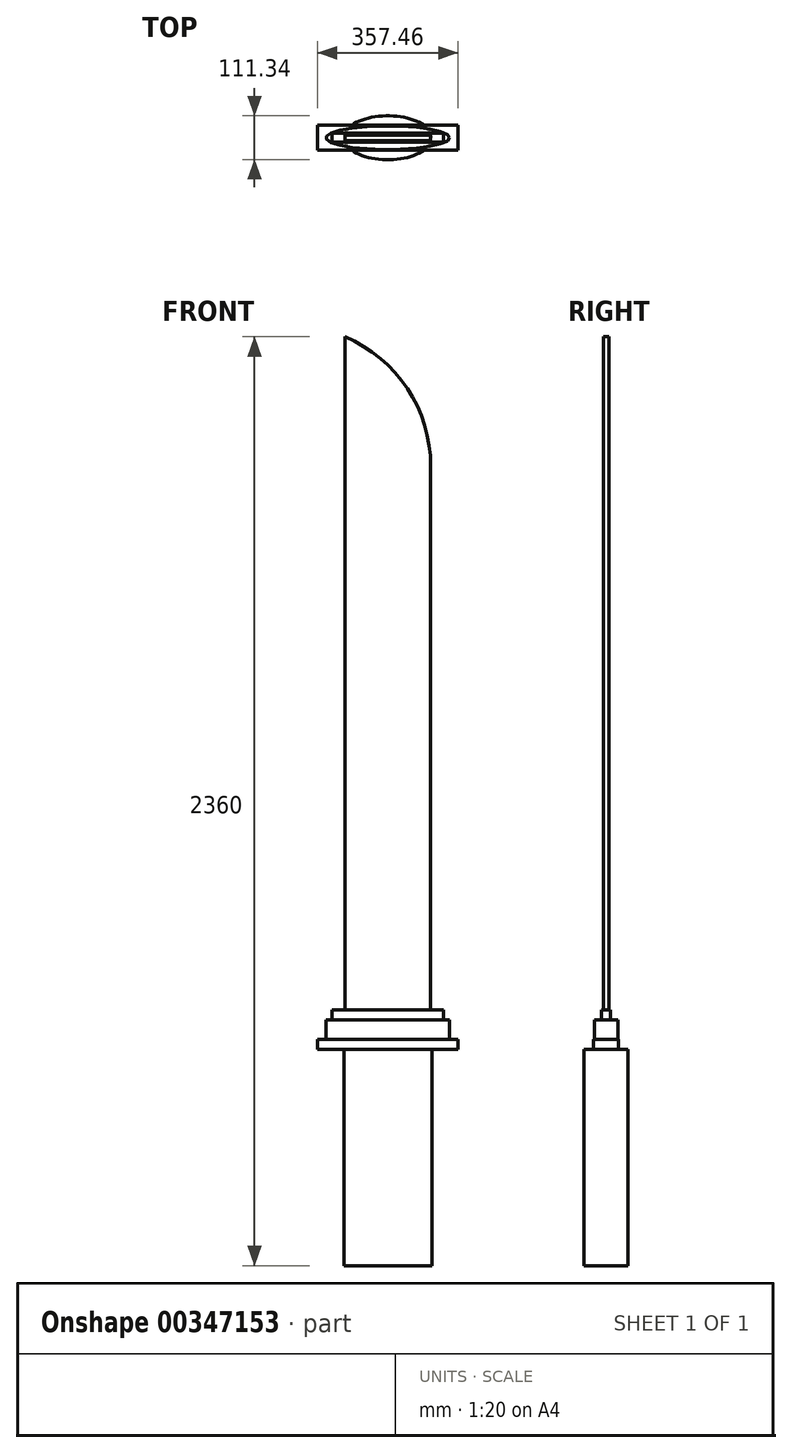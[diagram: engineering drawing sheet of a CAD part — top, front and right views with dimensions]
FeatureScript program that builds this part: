
annotation { "Feature Type Name" : "Feature", "Feature Type Description" : "" }
export const myFeature = defineFeature(function(context is Context, id is Id, definition is map)
    precondition{}
    {
        {
            var Q0;
            Q0=qCreatedBy(makeId("Top.planeOp"),FACE);
            var sketch = newSketch(context, id + "F0", { "sketchPlane" : qUnion([Q0])});
            skLineSegment(sketch, "E0.bottom", {"start": v(108.9, 6.8) * mm, "end": v(-108.9, 6.8) * mm});
            skLineSegment(sketch, "E0.top", {"start": v(108.9, -6.8) * mm, "end": v(-108.9, -6.8) * mm});
            skLineSegment(sketch, "E0.left", {"start": v(108.9, 6.8) * mm, "end": v(108.9, -6.8) * mm});
            skLineSegment(sketch, "E0.right", {"start": v(-108.9, 6.8) * mm, "end": v(-108.9, -6.8) * mm});
            skPoint(sketch, "E0.middle", {"position": v(0, 0) * mm});
            skSolve(sketch);
        }
        {
            var Q0;
            Q0=makeQuery(id+"F0.imprint","IMPRINT",FACE,{"disambiguationData":[TD([[makeQuery(id+"F0.imprint","IMPRINT",EDGE,{"derivedFrom":sQuery(id+"F0.wireOp",EDGE,"E0.bottom")}),1.0]])]});
            extrude(context, id + "F1", {"entities" : qUnion([Q0]), "depth" : 1710 * mm});
        }
        {
            var Q0;
            Q0=makeQuery(id+"F1.opExtrude","CAP_EDGE",EDGE,{"disambiguationData":[OSD([sQuery(id+"F0.wireOp",EDGE,"E0.left")])],"isStart":false});
            fillet(context, id + "F2", {"entities" : qUnion([Q0]), "radius" : 357.3 * mm, "tangentPropagation" : true, "allowEdgeOverflow" : false});
        }
        {
            var Q0;
            Q0=qCreatedBy(makeId("Top.planeOp"),FACE);
            var sketch = newSketch(context, id + "F3", { "sketchPlane" : qUnion([Q0])});
            skLineSegment(sketch, "E1.bottom", {"start": v(142.01, 11.57) * mm, "end": v(-142.01, 11.57) * mm});
            skLineSegment(sketch, "E1.top", {"start": v(142.01, -11.57) * mm, "end": v(-142.01, -11.57) * mm});
            skLineSegment(sketch, "E1.left", {"start": v(142.01, 11.57) * mm, "end": v(142.01, -11.57) * mm});
            skLineSegment(sketch, "E1.right", {"start": v(-142.01, 11.57) * mm, "end": v(-142.01, -11.57) * mm});
            skPoint(sketch, "E1.middle", {"position": v(0, 0) * mm});
            skSolve(sketch);
        }
        {
            var Q0;
            Q0=makeQuery(id+"F3.imprint","IMPRINT",FACE,{"disambiguationData":[TD([[makeQuery(id+"F3.imprint","IMPRINT",EDGE,{"derivedFrom":sQuery(id+"F3.wireOp",EDGE,"E1.bottom")}),1.0]])]});
            extrude(context, id + "F4", {"entities" : qUnion([Q0]), "operationType" : NewBodyOperationType.ADD, "oppositeDirection" : true, "depth" : 25 * mm});
        }
        {
            var Q0;
            Q0=qCreatedBy(makeId("Top.planeOp"),FACE);
            cPlane(context, id + "F5", {"entities" : qUnion([Q0]), "cplaneType" : CPlaneType.OFFSET, "offset" : 25 * mm, "oppositeDirection" : true, "width" : 150 * mm, "height" : 150 * mm});
        }
        {
            var Q0;
            Q0=qCreatedBy(id+"F5.planeOp",FACE);
            var sketch = newSketch(context, id + "F6", { "sketchPlane" : qUnion([Q0])});
            skEllipse(sketch, "E2", {"center": v(0, 0) * mm, "majorRadius": 157.13 * mm, "minorRadius": 29.95 * mm, "majorAxis": v(1, 0)});
            skSolve(sketch);
        }
        {
            var Q0;
            Q0=makeQuery(id+"F6.imprint","IMPRINT",FACE,{"disambiguationData":[TD([[makeQuery(id+"F6.imprint","IMPRINT",EDGE,{"derivedFrom":sQuery(id+"F6.wireOp",EDGE,"E2")}),1.0]])]});
            extrude(context, id + "F7", {"entities" : qUnion([Q0]), "operationType" : NewBodyOperationType.ADD, "oppositeDirection" : true, "depth" : 50 * mm});
        }
        {
            var Q0;
            Q0=qCreatedBy(id+"F5.planeOp",FACE);
            cPlane(context, id + "F8", {"entities" : qUnion([Q0]), "cplaneType" : CPlaneType.OFFSET, "offset" : 50 * mm, "oppositeDirection" : true, "width" : 150 * mm, "height" : 150 * mm});
        }
        {
            var Q0;
            Q0=qCreatedBy(id+"F8.planeOp",FACE);
            var sketch = newSketch(context, id + "F9", { "sketchPlane" : qUnion([Q0])});
            skLineSegment(sketch, "E3.bottom", {"start": v(178.73, -31.94) * mm, "end": v(-178.73, -31.94) * mm});
            skLineSegment(sketch, "E3.top", {"start": v(178.73, 31.94) * mm, "end": v(-178.73, 31.94) * mm});
            skLineSegment(sketch, "E3.left", {"start": v(178.73, -31.94) * mm, "end": v(178.73, 31.94) * mm});
            skLineSegment(sketch, "E3.right", {"start": v(-178.73, -31.94) * mm, "end": v(-178.73, 31.94) * mm});
            skPoint(sketch, "E3.middle", {"position": v(0, 0) * mm});
            skSolve(sketch);
        }
        {
            var Q0;
            Q0=makeQuery(id+"F9.imprint","IMPRINT",FACE,{"disambiguationData":[TD([[makeQuery(id+"F9.imprint","IMPRINT",EDGE,{"derivedFrom":sQuery(id+"F9.wireOp",EDGE,"E3.bottom")}),-1.0]])]});
            extrude(context, id + "F10", {"entities" : qUnion([Q0]), "operationType" : NewBodyOperationType.ADD, "oppositeDirection" : true, "depth" : 25 * mm});
        }
        {
            var Q0;
            Q0=qCreatedBy(id+"F8.planeOp",FACE);
            cPlane(context, id + "F11", {"entities" : qUnion([Q0]), "cplaneType" : CPlaneType.OFFSET, "offset" : 25 * mm, "oppositeDirection" : true, "width" : 150 * mm, "height" : 150 * mm});
        }
        {
            var Q0;
            Q0=qCreatedBy(id+"F11.planeOp",FACE);
            var sketch = newSketch(context, id + "F12", { "sketchPlane" : qUnion([Q0])});
            skEllipse(sketch, "E4", {"center": v(0, 0) * mm, "majorRadius": 111.75 * mm, "minorRadius": 55.67 * mm, "majorAxis": v(1, 0)});
            skSolve(sketch);
        }
        {
            var Q0;
            Q0=makeQuery(id+"F12.imprint","IMPRINT",FACE,{"disambiguationData":[TD([[makeQuery(id+"F12.imprint","IMPRINT",EDGE,{"derivedFrom":sQuery(id+"F12.wireOp",EDGE,"E4")}),1.0]])]});
            extrude(context, id + "F13", {"entities" : qUnion([Q0]), "operationType" : NewBodyOperationType.ADD, "oppositeDirection" : true, "depth" : 550 * mm});
        }
    });
